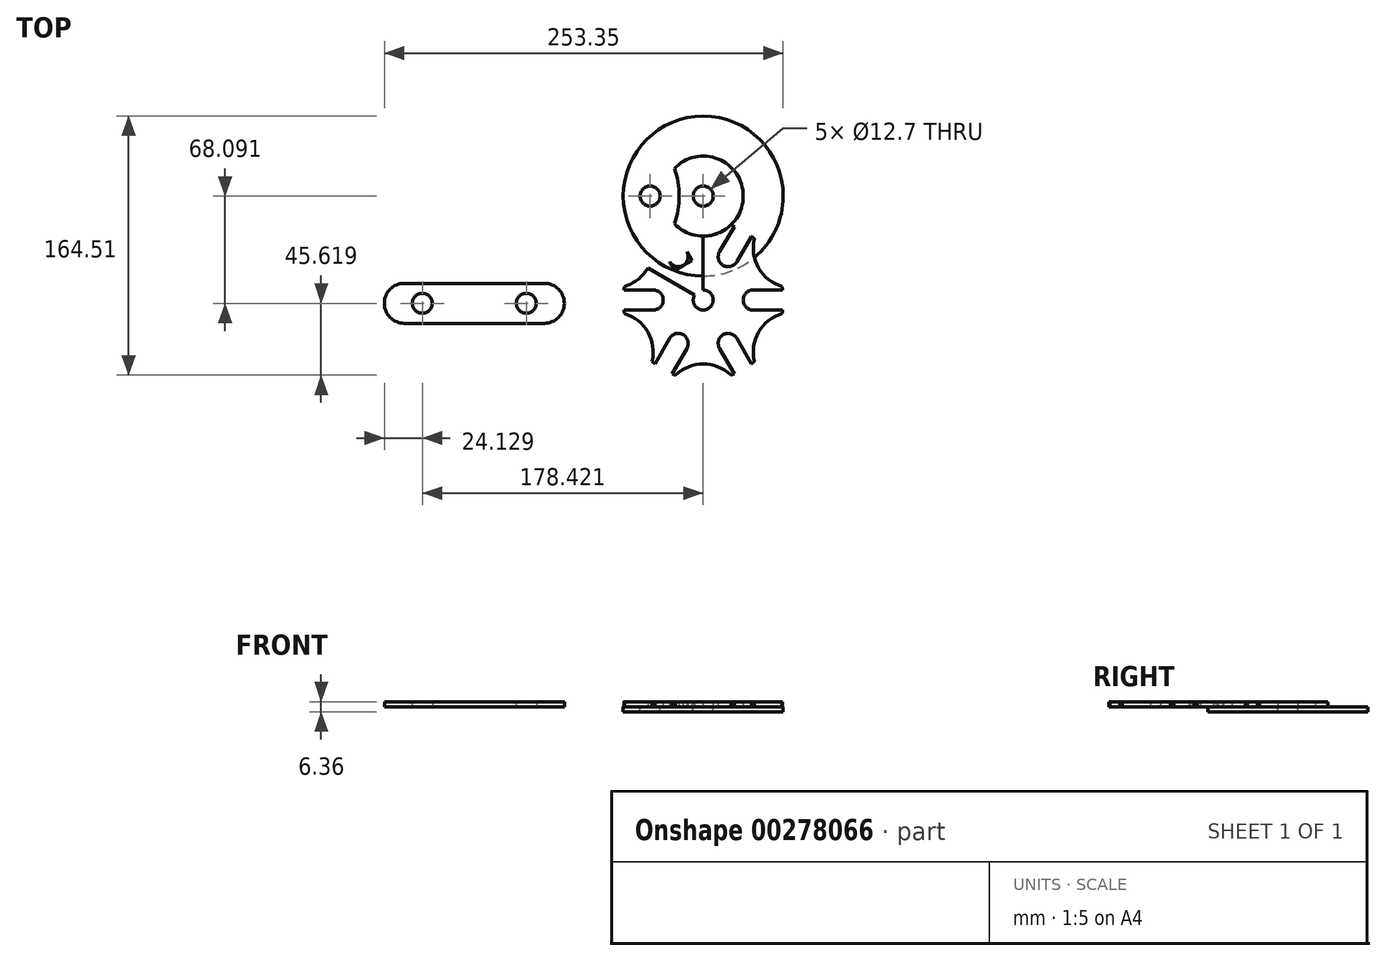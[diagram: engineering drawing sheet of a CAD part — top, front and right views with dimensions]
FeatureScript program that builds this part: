
annotation { "Feature Type Name" : "Feature", "Feature Type Description" : "" }
export const myFeature = defineFeature(function(context is Context, id is Id, definition is map)
    precondition{}
    {
        {
            var Q0;
            Q0=qCreatedBy(makeId("Top.planeOp"),FACE);
            var sketch = newSketch(context, id + "F0", { "sketchPlane" : qUnion([Q0])});
            skArc(sketch, "E0", {"start": v(-50.06, 8.64) * mm, "mid": v(-50.24, 7.5) * mm, "end": v(-50.4, 6.35) * mm});
            skLineSegment(sketch, "E1", {"start": v(0, 0) * mm, "end": v(0, 66.04) * mm});
            skLineSegment(sketch, "E2", {"start": v(0, 0) * mm, "end": v(57.2, 33.02) * mm});
            skLineSegment(sketch, "E3", {"start": v(0, 0) * mm, "end": v(57.2, -33.02) * mm});
            skLineSegment(sketch, "E4", {"start": v(0, 0) * mm, "end": v(0, -66.04) * mm});
            skLineSegment(sketch, "E5", {"start": v(0, 0) * mm, "end": v(-57.2, -33.02) * mm});
            skLineSegment(sketch, "E6", {"start": v(0, 0) * mm, "end": v(-57.2, 33.02) * mm});
            skArc(sketch, "E7", {"start": v(-17.55, 47.67) * mm, "mid": v(0, 40.64) * mm, "end": v(17.55, 47.67) * mm});
            skArc(sketch, "E8", {"start": v(32.51, 39.03) * mm, "mid": v(35.2, 20.32) * mm, "end": v(50.06, 8.64) * mm});
            skArc(sketch, "E9", {"start": v(50.06, -8.64) * mm, "mid": v(35.2, -20.32) * mm, "end": v(32.51, -39.03) * mm});
            skArc(sketch, "E10", {"start": v(17.55, -47.67) * mm, "mid": v(0, -40.64) * mm, "end": v(-17.55, -47.67) * mm});
            skArc(sketch, "E11", {"start": v(-32.51, -39.03) * mm, "mid": v(-35.2, -20.32) * mm, "end": v(-50.06, -8.64) * mm});
            skArc(sketch, "E12", {"start": v(-50.06, 8.64) * mm, "mid": v(-35.2, 20.32) * mm, "end": v(-32.51, 39.03) * mm});
            skArc(sketch, "E13.trimOffspring", {"start": v(-17.55, 47.67) * mm, "mid": v(-18.63, 47.26) * mm, "end": v(-19.7, 46.82) * mm});
            skArc(sketch, "E14.trimOffspring", {"start": v(32.51, 39.03) * mm, "mid": v(31.62, 39.76) * mm, "end": v(30.7, 40.47) * mm});
            skArc(sketch, "E15.trimOffspring", {"start": v(50.06, -8.64) * mm, "mid": v(50.24, -7.5) * mm, "end": v(50.4, -6.35) * mm});
            skArc(sketch, "E16.trimOffspring", {"start": v(17.55, -47.67) * mm, "mid": v(18.63, -47.26) * mm, "end": v(19.7, -46.83) * mm});
            skArc(sketch, "E17.trimOffspring", {"start": v(-32.51, -39.03) * mm, "mid": v(-31.61, -39.77) * mm, "end": v(-30.7, -40.48) * mm});
            skLineSegment(sketch, "E18", {"start": v(7.2, 25.17) * mm, "end": v(18.2, 18.82) * mm});
            skLineSegment(sketch, "E19", {"start": v(7.2, 25.17) * mm, "end": v(19.7, 46.82) * mm});
            skLineSegment(sketch, "E20", {"start": v(18.2, 18.82) * mm, "end": v(30.7, 40.47) * mm});
            skArc(sketch, "E21.trimOffspring", {"start": v(19.7, 46.82) * mm, "mid": v(18.63, 47.26) * mm, "end": v(17.55, 47.67) * mm});
            skLineSegment(sketch, "E22", {"start": v(25.4, 6.35) * mm, "end": v(25.4, -6.35) * mm});
            skLineSegment(sketch, "E23", {"start": v(25.4, 6.35) * mm, "end": v(50.4, 6.35) * mm});
            skLineSegment(sketch, "E24", {"start": v(25.4, -6.35) * mm, "end": v(50.4, -6.35) * mm});
            skArc(sketch, "E25.trimOffspring", {"start": v(50.4, 6.35) * mm, "mid": v(50.24, 7.5) * mm, "end": v(50.06, 8.64) * mm});
            skLineSegment(sketch, "E26", {"start": v(18.2, -18.83) * mm, "end": v(7.2, -25.18) * mm});
            skLineSegment(sketch, "E27", {"start": v(7.2, -25.18) * mm, "end": v(19.7, -46.83) * mm});
            skLineSegment(sketch, "E28", {"start": v(18.2, -18.83) * mm, "end": v(30.7, -40.48) * mm});
            skArc(sketch, "E29.trimOffspring", {"start": v(30.7, -40.48) * mm, "mid": v(31.61, -39.77) * mm, "end": v(32.51, -39.03) * mm});
            skLineSegment(sketch, "E30", {"start": v(-7.2, -25.18) * mm, "end": v(-18.2, -18.83) * mm});
            skLineSegment(sketch, "E31", {"start": v(-18.2, -18.83) * mm, "end": v(-30.7, -40.48) * mm});
            skLineSegment(sketch, "E32", {"start": v(-7.2, -25.18) * mm, "end": v(-19.7, -46.83) * mm});
            skArc(sketch, "E33.trimOffspring", {"start": v(-19.7, -46.83) * mm, "mid": v(-18.63, -47.26) * mm, "end": v(-17.55, -47.67) * mm});
            skLineSegment(sketch, "E34", {"start": v(-25.4, -6.35) * mm, "end": v(-25.4, 6.35) * mm});
            skLineSegment(sketch, "E35", {"start": v(-25.4, 6.35) * mm, "end": v(-50.4, 6.35) * mm});
            skLineSegment(sketch, "E36", {"start": v(-25.4, -6.35) * mm, "end": v(-50.4, -6.35) * mm});
            skArc(sketch, "E37.trimOffspring", {"start": v(-50.4, -6.35) * mm, "mid": v(-50.24, -7.5) * mm, "end": v(-50.06, -8.64) * mm});
            skLineSegment(sketch, "E38", {"start": v(-30.7, 40.47) * mm, "end": v(-18.2, 18.82) * mm});
            skLineSegment(sketch, "E39", {"start": v(-18.2, 18.82) * mm, "end": v(-7.2, 25.17) * mm});
            skLineSegment(sketch, "E40", {"start": v(-7.2, 25.17) * mm, "end": v(-19.7, 46.82) * mm});
            skArc(sketch, "E41.trimOffspring", {"start": v(-30.7, 40.47) * mm, "mid": v(-31.62, 39.76) * mm, "end": v(-32.51, 39.03) * mm});
            skCircle(sketch, "E42", {"center": v(0, 0) * mm, "radius": 6.35 * mm});
            skLineSegment(sketch, "E43", {"start": v(-18.2, 18.82) * mm, "end": v(-30.7, 40.47) * mm});
            skArc(sketch, "E44", {"start": v(10.38, 30.67) * mm, "mid": v(12.7, 22) * mm, "end": v(21.37, 24.32) * mm});
            skPoint(sketch, "E45", {"position": v(10.38, 30.67) * mm});
            skPoint(sketch, "E46", {"position": v(21.37, 24.32) * mm});
            skArc(sketch, "E47", {"start": v(31.75, 6.35) * mm, "mid": v(25.4, 0) * mm, "end": v(31.75, -6.35) * mm});
            skPoint(sketch, "E48", {"position": v(31.75, 6.35) * mm});
            skPoint(sketch, "E49", {"position": v(31.75, -6.35) * mm});
            skArc(sketch, "E50", {"start": v(21.37, -24.32) * mm, "mid": v(12.7, -22) * mm, "end": v(10.37, -30.67) * mm});
            skPoint(sketch, "E51", {"position": v(10.37, -30.67) * mm});
            skPoint(sketch, "E52", {"position": v(21.37, -24.32) * mm});
            skArc(sketch, "E53", {"start": v(-10.37, -30.67) * mm, "mid": v(-12.7, -22) * mm, "end": v(-21.37, -24.32) * mm});
            skPoint(sketch, "E54", {"position": v(-21.37, -24.32) * mm});
            skPoint(sketch, "E55", {"position": v(-10.37, -30.67) * mm});
            skArc(sketch, "E56", {"start": v(-31.75, -6.35) * mm, "mid": v(-25.4, 0) * mm, "end": v(-31.75, 6.35) * mm});
            skPoint(sketch, "E57", {"position": v(-31.75, 6.35) * mm});
            skPoint(sketch, "E58", {"position": v(-31.75, -6.35) * mm});
            skArc(sketch, "E59", {"start": v(-21.38, 24.32) * mm, "mid": v(-12.7, 22) * mm, "end": v(-10.38, 30.67) * mm});
            skPoint(sketch, "E60", {"position": v(-21.38, 24.32) * mm});
            skPoint(sketch, "E61", {"position": v(-10.38, 30.67) * mm});
            skSolve(sketch);
        }
        {
            var Q0;
            Q0=makeQuery(id+"F0.imprint","IMPRINT",FACE,{"disambiguationData":[TD([[makeQuery(id+"F0.imprint","IMPRINT",EDGE,{"derivedFrom":sQuery(id+"F0.wireOp",EDGE,"E18")}),-1.0]])]});
            var Q1;
            {var subQ0=sQuery(id+"F0.wireOp",EDGE,"E13.trimOffspring");Q1=makeQuery(id+"F0.imprint","IMPRINT",FACE,{"disambiguationData":[TD([[makeQuery(id+"F0.imprint","IMPRINT",EDGE,{"derivedFrom":subQ0}),1.0]])]});}
            var Q2;
            {var subQ0=sQuery(id+"F0.wireOp",EDGE,"E0");Q2=makeQuery(id+"F0.imprint","IMPRINT",FACE,{"disambiguationData":[TD([[makeQuery(id+"F0.imprint","IMPRINT",EDGE,{"derivedFrom":subQ0}),1.0]])]});}
            var Q3;
            {var subQ0=sQuery(id+"F0.wireOp",EDGE,"E17.trimOffspring");Q3=makeQuery(id+"F0.imprint","IMPRINT",FACE,{"disambiguationData":[TD([[makeQuery(id+"F0.imprint","IMPRINT",EDGE,{"derivedFrom":subQ0}),1.0]])]});}
            var Q4;
            {var subQ0=sQuery(id+"F0.wireOp",EDGE,"E16.trimOffspring");Q4=makeQuery(id+"F0.imprint","IMPRINT",FACE,{"disambiguationData":[TD([[makeQuery(id+"F0.imprint","IMPRINT",EDGE,{"derivedFrom":subQ0}),1.0]])]});}
            var Q5;
            {var subQ0=sQuery(id+"F0.wireOp",EDGE,"E15.trimOffspring");Q5=makeQuery(id+"F0.imprint","IMPRINT",FACE,{"disambiguationData":[TD([[makeQuery(id+"F0.imprint","IMPRINT",EDGE,{"derivedFrom":subQ0}),1.0]])]});}
            var Q6;
            {var subQ0=sQuery(id+"F0.wireOp",EDGE,"E35");var subQ1=sQuery(id+"F0.wireOp",EDGE,"E34");var subQ2=makeQuery(id+"F0.imprint","INTERSECT",VERTEX,{"derivedFrom":[subQ1,subQ0]});Q6=makeQuery(id+"F0.imprint","IMPRINT",FACE,{"disambiguationData":[TD([[makeQuery(id+"F0.imprint","IMPRINT",EDGE,{"disambiguationData":[TD([[subQ2,1.0]])],"derivedFrom":subQ1}),1.0]])]});}
            var Q7;
            {var subQ0=sQuery(id+"F0.wireOp",EDGE,"E36");var subQ1=sQuery(id+"F0.wireOp",EDGE,"E34");var subQ2=makeQuery(id+"F0.imprint","INTERSECT",VERTEX,{"derivedFrom":[subQ1,subQ0]});Q7=makeQuery(id+"F0.imprint","IMPRINT",FACE,{"disambiguationData":[TD([[makeQuery(id+"F0.imprint","IMPRINT",EDGE,{"disambiguationData":[TD([[subQ2,-1.0]])],"derivedFrom":subQ1}),1.0]])]});}
            var Q8;
            {var subQ0=sQuery(id+"F0.wireOp",EDGE,"E43");var subQ1=sQuery(id+"F0.wireOp",EDGE,"E39");var subQ2=makeQuery(id+"F0.imprint","INTERSECT",VERTEX,{"derivedFrom":[subQ1,subQ0]});Q8=makeQuery(id+"F0.imprint","IMPRINT",FACE,{"disambiguationData":[TD([[makeQuery(id+"F0.imprint","IMPRINT",EDGE,{"disambiguationData":[TD([[subQ2,-1.0]])],"derivedFrom":subQ1}),1.0]])]});}
            var Q9;
            {var subQ0=sQuery(id+"F0.wireOp",EDGE,"E40");var subQ1=sQuery(id+"F0.wireOp",EDGE,"E39");var subQ2=makeQuery(id+"F0.imprint","INTERSECT",VERTEX,{"derivedFrom":[subQ1,subQ0]});Q9=makeQuery(id+"F0.imprint","IMPRINT",FACE,{"disambiguationData":[TD([[makeQuery(id+"F0.imprint","IMPRINT",EDGE,{"disambiguationData":[TD([[subQ2,1.0]])],"derivedFrom":subQ1}),1.0]])]});}
            var Q10;
            {var subQ0=sQuery(id+"F0.wireOp",EDGE,"E19");var subQ1=sQuery(id+"F0.wireOp",EDGE,"E18");var subQ2=makeQuery(id+"F0.imprint","INTERSECT",VERTEX,{"derivedFrom":[subQ1,subQ0]});Q10=makeQuery(id+"F0.imprint","IMPRINT",FACE,{"disambiguationData":[TD([[makeQuery(id+"F0.imprint","IMPRINT",EDGE,{"disambiguationData":[TD([[subQ2,-1.0]])],"derivedFrom":subQ1}),1.0]])]});}
            var Q11;
            {var subQ0=sQuery(id+"F0.wireOp",EDGE,"E20");var subQ1=sQuery(id+"F0.wireOp",EDGE,"E18");var subQ2=makeQuery(id+"F0.imprint","INTERSECT",VERTEX,{"derivedFrom":[subQ1,subQ0]});Q11=makeQuery(id+"F0.imprint","IMPRINT",FACE,{"disambiguationData":[TD([[makeQuery(id+"F0.imprint","IMPRINT",EDGE,{"disambiguationData":[TD([[subQ2,1.0]])],"derivedFrom":subQ1}),1.0]])]});}
            var Q12;
            {var subQ0=sQuery(id+"F0.wireOp",EDGE,"E23");var subQ1=sQuery(id+"F0.wireOp",EDGE,"E22");var subQ2=makeQuery(id+"F0.imprint","INTERSECT",VERTEX,{"derivedFrom":[subQ1,subQ0]});Q12=makeQuery(id+"F0.imprint","IMPRINT",FACE,{"disambiguationData":[TD([[makeQuery(id+"F0.imprint","IMPRINT",EDGE,{"disambiguationData":[TD([[subQ2,-1.0]])],"derivedFrom":subQ1}),1.0]])]});}
            var Q13;
            {var subQ0=sQuery(id+"F0.wireOp",EDGE,"E24");var subQ1=sQuery(id+"F0.wireOp",EDGE,"E22");var subQ2=makeQuery(id+"F0.imprint","INTERSECT",VERTEX,{"derivedFrom":[subQ1,subQ0]});Q13=makeQuery(id+"F0.imprint","IMPRINT",FACE,{"disambiguationData":[TD([[makeQuery(id+"F0.imprint","IMPRINT",EDGE,{"disambiguationData":[TD([[subQ2,1.0]])],"derivedFrom":subQ1}),1.0]])]});}
            var Q14;
            {var subQ0=sQuery(id+"F0.wireOp",EDGE,"E28");var subQ1=sQuery(id+"F0.wireOp",EDGE,"E26");var subQ2=makeQuery(id+"F0.imprint","INTERSECT",VERTEX,{"derivedFrom":[subQ1,subQ0]});Q14=makeQuery(id+"F0.imprint","IMPRINT",FACE,{"disambiguationData":[TD([[makeQuery(id+"F0.imprint","IMPRINT",EDGE,{"disambiguationData":[TD([[subQ2,-1.0]])],"derivedFrom":subQ1}),1.0]])]});}
            var Q15;
            {var subQ0=sQuery(id+"F0.wireOp",EDGE,"E27");var subQ1=sQuery(id+"F0.wireOp",EDGE,"E26");var subQ2=makeQuery(id+"F0.imprint","INTERSECT",VERTEX,{"derivedFrom":[subQ1,subQ0]});Q15=makeQuery(id+"F0.imprint","IMPRINT",FACE,{"disambiguationData":[TD([[makeQuery(id+"F0.imprint","IMPRINT",EDGE,{"disambiguationData":[TD([[subQ2,1.0]])],"derivedFrom":subQ1}),1.0]])]});}
            var Q16;
            {var subQ0=sQuery(id+"F0.wireOp",EDGE,"E32");var subQ1=sQuery(id+"F0.wireOp",EDGE,"E30");var subQ2=makeQuery(id+"F0.imprint","INTERSECT",VERTEX,{"derivedFrom":[subQ1,subQ0]});Q16=makeQuery(id+"F0.imprint","IMPRINT",FACE,{"disambiguationData":[TD([[makeQuery(id+"F0.imprint","IMPRINT",EDGE,{"disambiguationData":[TD([[subQ2,-1.0]])],"derivedFrom":subQ1}),1.0]])]});}
            var Q17;
            {var subQ0=sQuery(id+"F0.wireOp",EDGE,"E31");var subQ1=sQuery(id+"F0.wireOp",EDGE,"E30");var subQ2=makeQuery(id+"F0.imprint","INTERSECT",VERTEX,{"derivedFrom":[subQ1,subQ0]});Q17=makeQuery(id+"F0.imprint","IMPRINT",FACE,{"disambiguationData":[TD([[makeQuery(id+"F0.imprint","IMPRINT",EDGE,{"disambiguationData":[TD([[subQ2,1.0]])],"derivedFrom":subQ1}),1.0]])]});}
            extrude(context, id + "F1", {"entities" : qUnion([Q0, Q1, Q2, Q3, Q4, Q5, Q6, Q7, Q8, Q9, Q10, Q11, Q12, Q13, Q14, Q15, Q16, Q17]), "depth" : 3.17 * mm});
        }
        {
            var Q0;
            Q0=qCreatedBy(makeId("Top.planeOp"),FACE);
            var sketch = newSketch(context, id + "F2", { "sketchPlane" : qUnion([Q0])});
            skCircle(sketch, "E62", {"center": v(0, 66.04) * mm, "radius": 50.8 * mm});
            skCircle(sketch, "E63", {"center": v(0, 66.04) * mm, "radius": 6.35 * mm});
            skSolve(sketch);
        }
        {
            var Q0;
            Q0=makeQuery(id+"F2.imprint","IMPRINT",FACE,{"disambiguationData":[TD([[makeQuery(id+"F2.imprint","IMPRINT",EDGE,{"derivedFrom":sQuery(id+"F2.wireOp",EDGE,"E62")}),1.0]])]});
            extrude(context, id + "F3", {"entities" : qUnion([Q0]), "oppositeDirection" : true, "depth" : 3.17 * mm});
        }
        {
            var Q0;
            Q0=makeQuery(id+"F3.opExtrude","CAP_FACE",FACE,{"disambiguationData":[OSD([sQuery(id+"F2.wireOp",EDGE,"E62")])],"isStart":true});
            var sketch = newSketch(context, id + "F4", { "sketchPlane" : qUnion([Q0])});
            skArc(sketch, "E64", {"start": v(-18.37, 48.5) * mm, "mid": v(25.4, 66.04) * mm, "end": v(-18.37, 83.59) * mm});
            skArc(sketch, "E65", {"start": v(-18.37, 48.5) * mm, "mid": v(-15.24, 66.04) * mm, "end": v(-18.37, 83.59) * mm});
            skCircle(sketch, "E66", {"center": v(0, 66.04) * mm, "radius": 6.35 * mm});
            skCircle(sketch, "E67", {"center": v(-33.7, 66.04) * mm, "radius": 6.35 * mm});
            skPoint(sketch, "E67.centerSnap0", {"position": v(-15.24, 66.04) * mm});
            skSolve(sketch);
        }
        {
            var Q0;
            {var subQ0=sQuery(id+"F4.wireOp",EDGE,"E65");Q0=makeQuery(id+"F4.imprint","IMPRINT",FACE,{"disambiguationData":[TD([[makeQuery(id+"F4.imprint","IMPRINT",EDGE,{"derivedFrom":subQ0}),-1.0]])]});}
            extrude(context, id + "F5", {"entities" : qUnion([Q0]), "depth" : 3.17 * mm});
        }
        {
            var Q0;
            Q0=qCreatedBy(makeId("Top.planeOp"),FACE);
            var sketch = newSketch(context, id + "F6", { "sketchPlane" : qUnion([Q0])});
            skLineSegment(sketch, "E68", {"start": v(-189.85, -14.75) * mm, "end": v(-100.95, -14.75) * mm});
            skLineSegment(sketch, "E69", {"start": v(-189.85, 10.65) * mm, "end": v(-100.95, 10.65) * mm});
            skCircle(sketch, "E70", {"center": v(-178.42, -2.05) * mm, "radius": 6.35 * mm});
            skCircle(sketch, "E71", {"center": v(-112.38, -2.05) * mm, "radius": 6.35 * mm});
            skArc(sketch, "E72", {"start": v(-100.95, -14.75) * mm, "mid": v(-88.25, -2.05) * mm, "end": v(-100.95, 10.65) * mm});
            skArc(sketch, "E73", {"start": v(-189.85, 10.65) * mm, "mid": v(-202.55, -2.05) * mm, "end": v(-189.85, -14.75) * mm});
            skSolve(sketch);
        }
        {
            var Q0;
            Q0=makeQuery(id+"F6.imprint","IMPRINT",FACE,{"disambiguationData":[TD([[makeQuery(id+"F6.imprint","IMPRINT",EDGE,{"derivedFrom":sQuery(id+"F6.wireOp",EDGE,"E68")}),1.0]])]});
            extrude(context, id + "F7", {"entities" : qUnion([Q0]), "depth" : 3.17 * mm});
        }
        {
            var Q0;
            Q0=makeQuery(id+"F4.imprint","IMPRINT",FACE,{"disambiguationData":[TD([[makeQuery(id+"F4.imprint","IMPRINT",EDGE,{"derivedFrom":sQuery(id+"F4.wireOp",EDGE,"E67")}),1.0]])]});
            extrude(context, id + "F8", {"entities" : qUnion([Q0]), "operationType" : NewBodyOperationType.REMOVE, "endBound" : BoundingType.THROUGH_ALL, "oppositeDirection" : true, "depth" : 25.4 * mm});
        }
    });
